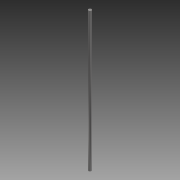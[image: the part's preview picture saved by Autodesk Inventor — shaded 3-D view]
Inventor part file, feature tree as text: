
AUTODESK INVENTOR PART (.ipt)
format: ipt  version: 2013 (Build 170138000, 138)  size: 74,240 bytes
history: native  units: mm
features: extrude x1, sketch x1
ambient origin geometry x8: Origin, YZ Plane, XZ Plane, XY Plane, X Axis, Y Axis, Z Axis, Center Point
bodies: Solid1 (feature_tree)
feature tree (2):
  extrude  "Extrusion1"  Depth=369.0mm TaperAngle=0.0deg
  sketch  "Sketch1"  dims[d0=8.0mm d2=369.0mm d3=0.0mm]
